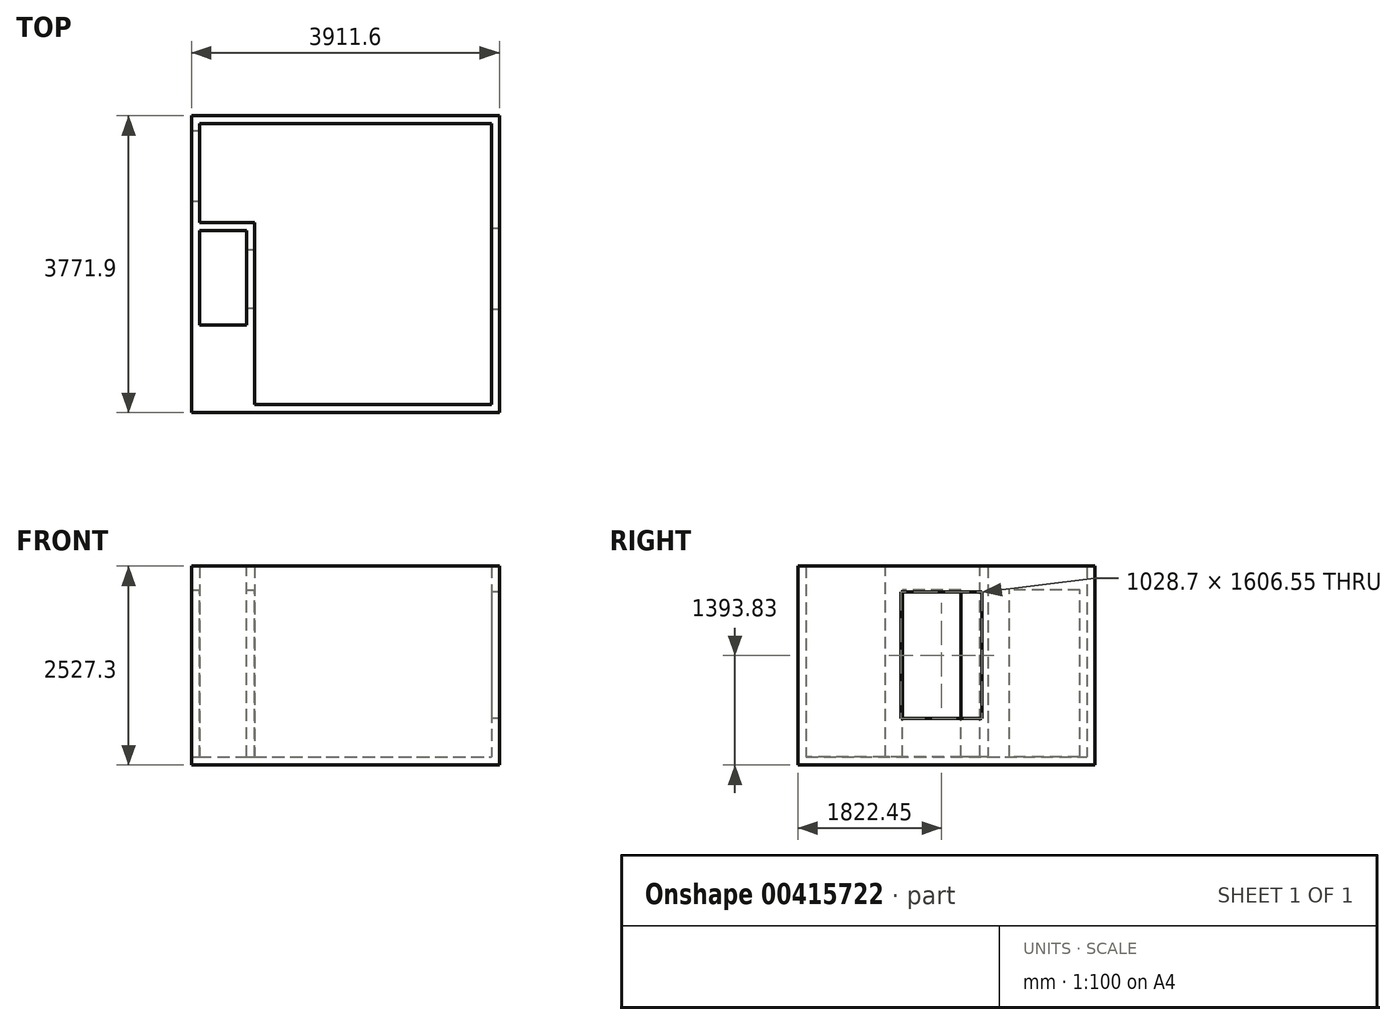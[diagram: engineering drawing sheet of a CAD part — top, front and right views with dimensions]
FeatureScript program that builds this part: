
annotation { "Feature Type Name" : "Feature", "Feature Type Description" : "" }
export const myFeature = defineFeature(function(context is Context, id is Id, definition is map)
    precondition{}
    {
        {
            var Q0;
            Q0=qCreatedBy(makeId("Top.planeOp"),FACE);
            var sketch = newSketch(context, id + "F0", { "sketchPlane" : qUnion([Q0])});
            skLineSegment(sketch, "E0.bottom", {"start": v(701.67, 0) * mm, "end": v(3708.4, 0) * mm});
            skLineSegment(sketch, "E0.top", {"start": v(0, 3568.7) * mm, "end": v(3708.4, 3568.7) * mm});
            skLineSegment(sketch, "E0.left", {"start": v(0, 2314.58) * mm, "end": v(0, 3568.7) * mm});
            skLineSegment(sketch, "E0.right", {"start": v(3708.4, 0) * mm, "end": v(3708.4, 3568.7) * mm});
            skLineSegment(sketch, "E1.0", {"start": v(-101.6, -101.6) * mm, "end": v(-101.6, 3670.3) * mm});
            skLineSegment(sketch, "E1.1", {"start": v(-101.6, -101.6) * mm, "end": v(3810, -101.6) * mm});
            skLineSegment(sketch, "E1.2", {"start": v(3810, -101.6) * mm, "end": v(3810, 3670.3) * mm});
            skLineSegment(sketch, "E1.3", {"start": v(-101.6, 3670.3) * mm, "end": v(3810, 3670.3) * mm});
            skLineSegment(sketch, "E2", {"start": v(0, 2314.58) * mm, "end": v(701.67, 2314.58) * mm});
            skLineSegment(sketch, "E3", {"start": v(701.67, 2314.58) * mm, "end": v(701.67, 0) * mm});
            skSolve(sketch);
        }
        {
            var Q0;
            Q0=qSketchRegion(id+"F0",true);
            extrude(context, id + "F1", {"entities" : qUnion([Q0]), "offsetDistance" : 25.4 * mm, "depth" : 2425.7 * mm});
        }
        {
            var Q0;
            Q0=makeQuery(id+"F1.opExtrude","CAP_FACE",FACE,{"disambiguationData":[OSD([sQuery(id+"F0.wireOp",EDGE,"E0.bottom"),sQuery(id+"F0.wireOp",EDGE,"E0.top"),sQuery(id+"F0.wireOp",EDGE,"E0.left"),sQuery(id+"F0.wireOp",EDGE,"E0.right"),sQuery(id+"F0.wireOp",EDGE,"E1.0"),sQuery(id+"F0.wireOp",EDGE,"E1.1"),sQuery(id+"F0.wireOp",EDGE,"E1.2"),sQuery(id+"F0.wireOp",EDGE,"E1.3")])],"isStart":true});
            var sketch = newSketch(context, id + "F2", { "sketchPlane" : qUnion([Q0])});
            skLineSegment(sketch, "E4.0", {"start": v(-101.6, 101.6) * mm, "end": v(3810, 101.6) * mm});
            skLineSegment(sketch, "E5.0", {"start": v(-101.6, 101.6) * mm, "end": v(-101.6, -3670.3) * mm});
            skLineSegment(sketch, "E6.0", {"start": v(-101.6, -3670.3) * mm, "end": v(3810, -3670.3) * mm});
            skLineSegment(sketch, "E7.0", {"start": v(3810, 101.6) * mm, "end": v(3810, -3670.3) * mm});
            skSolve(sketch);
        }
        {
            var Q0;
            Q0=qSketchRegion(id+"F2",true);
            extrude(context, id + "F3", {"entities" : qUnion([Q0]), "operationType" : NewBodyOperationType.ADD, "offsetDistance" : 25.4 * mm, "depth" : 101.6 * mm});
        }
        {
            var Q0;
            Q0=makeQuery(id+"F1.opExtrude","SWEPT_FACE",FACE,{"disambiguationData":[OSD([sQuery(id+"F0.wireOp",EDGE,"E0.left")])]});
            var sketch = newSketch(context, id + "F4", { "sketchPlane" : qUnion([Q0])});
            skLineSegment(sketch, "E8.bottom", {"start": v(3479.8, 0) * mm, "end": v(2584.45, 0) * mm});
            skLineSegment(sketch, "E8.top", {"start": v(3479.8, 2120.9) * mm, "end": v(2584.45, 2120.9) * mm});
            skLineSegment(sketch, "E8.left", {"start": v(3479.8, 0) * mm, "end": v(3479.8, 2120.9) * mm});
            skLineSegment(sketch, "E8.right", {"start": v(2584.45, 0) * mm, "end": v(2584.45, 2120.9) * mm});
            skSolve(sketch);
        }
        {
            var Q0;
            Q0=qSketchRegion(id+"F4",true);
            extrude(context, id + "F5", {"entities" : qUnion([Q0]), "operationType" : NewBodyOperationType.REMOVE, "endBound" : BoundingType.THROUGH_ALL, "oppositeDirection" : true, "offsetDistance" : 25.4 * mm, "depth" : 25.4 * mm});
        }
        {
            var Q0;
            Q0=makeQuery(id+"F1.opExtrude","SWEPT_FACE",FACE,{"disambiguationData":[OSD([sQuery(id+"F0.wireOp",EDGE,"E0.right")])]});
            var sketch = newSketch(context, id + "F6", { "sketchPlane" : qUnion([Q0])});
            skLineSegment(sketch, "E9.bottom", {"start": v(-2235.2, 2095.5) * mm, "end": v(-1206.5, 2095.5) * mm});
            skLineSegment(sketch, "E9.top", {"start": v(-2235.2, 488.95) * mm, "end": v(-1206.5, 488.95) * mm});
            skLineSegment(sketch, "E9.left", {"start": v(-2235.2, 2095.5) * mm, "end": v(-2235.2, 488.95) * mm});
            skLineSegment(sketch, "E9.right", {"start": v(-1206.5, 2095.5) * mm, "end": v(-1206.5, 488.95) * mm});
            skSolve(sketch);
        }
        {
            var Q0;
            Q0=qSketchRegion(id+"F6",true);
            extrude(context, id + "F7", {"entities" : qUnion([Q0]), "operationType" : NewBodyOperationType.REMOVE, "endBound" : BoundingType.THROUGH_ALL, "oppositeDirection" : true, "offsetDistance" : 25.4 * mm, "depth" : 25.4 * mm});
        }
        {
            var Q0;
            Q0=makeQuery(id+"F1.opExtrude","SWEPT_FACE",FACE,{"disambiguationData":[OSD([sQuery(id+"F0.wireOp",EDGE,"E3")])]});
            var sketch = newSketch(context, id + "F8", { "sketchPlane" : qUnion([Q0])});
            skLineSegment(sketch, "E10.bottom", {"start": v(1968.5, 0) * mm, "end": v(1228.73, 0) * mm});
            skLineSegment(sketch, "E10.top", {"start": v(1968.5, 2120.9) * mm, "end": v(1228.73, 2120.9) * mm});
            skLineSegment(sketch, "E10.left", {"start": v(1968.5, 0) * mm, "end": v(1968.5, 2120.9) * mm});
            skLineSegment(sketch, "E10.right", {"start": v(1228.73, 0) * mm, "end": v(1228.73, 2120.9) * mm});
            skSolve(sketch);
        }
        {
            var Q0;
            Q0 = qSketchRegion(id + "F8", true);
            extrude(context, id + "F9", {"entities" : qUnion([Q0]), "operationType" : NewBodyOperationType.REMOVE, "oppositeDirection" : true, "offsetDistance" : 25.4 * mm, "depth" : 101.6 * mm});
        }
        {
            var Q0;
            Q0=makeQuery(id+"F1.opExtrude","CAP_FACE",FACE,{"disambiguationData":[OSD([sQuery(id+"F0.wireOp",EDGE,"E0.bottom"),sQuery(id+"F0.wireOp",EDGE,"E0.top"),sQuery(id+"F0.wireOp",EDGE,"E0.left"),sQuery(id+"F0.wireOp",EDGE,"E0.right"),sQuery(id+"F0.wireOp",EDGE,"E1.0"),sQuery(id+"F0.wireOp",EDGE,"E1.1"),sQuery(id+"F0.wireOp",EDGE,"E1.2"),sQuery(id+"F0.wireOp",EDGE,"E1.3"),sQuery(id+"F0.wireOp",EDGE,"E2"),sQuery(id+"F0.wireOp",EDGE,"E3")])],"isStart":false});
            var sketch = newSketch(context, id + "F10", { "sketchPlane" : qUnion([Q0])});
            skLineSegment(sketch, "E11.bottom", {"start": v(0, 2212.98) * mm, "end": v(600.07, 2212.98) * mm});
            skLineSegment(sketch, "E11.top", {"start": v(0, 1012.83) * mm, "end": v(600.07, 1012.83) * mm});
            skLineSegment(sketch, "E11.left", {"start": v(0, 2212.98) * mm, "end": v(0, 1012.83) * mm});
            skLineSegment(sketch, "E11.right", {"start": v(600.07, 2212.98) * mm, "end": v(600.07, 1012.83) * mm});
            skSolve(sketch);
        }
        {
            var Q0;
            Q0 = qSketchRegion(id + "F10", true);
            var Q1;
            Q1=makeQuery(id+"F9.boolean.opBoolean","MERGE",FACE,{"derivedFrom":[makeQuery(id+"F5.boolean.opBoolean","MERGE",FACE,{"derivedFrom":[makeQuery(id+"F3.opExtrude","CAP_FACE",FACE,{"disambiguationData":[OSD([sQuery(id+"F2.wireOp",EDGE,"E4.0"),sQuery(id+"F2.wireOp",EDGE,"E5.0"),sQuery(id+"F2.wireOp",EDGE,"E6.0"),sQuery(id+"F2.wireOp",EDGE,"E7.0")])],"isStart":true}),makeQuery(id+"F5.opExtrude","SWEPT_FACE",FACE,{"disambiguationData":[OSD([sQuery(id+"F4.wireOp",EDGE,"E8.bottom")])]})]}),makeQuery(id+"F9.opExtrude","SWEPT_FACE",FACE,{"disambiguationData":[OSD([sQuery(id+"F8.wireOp",EDGE,"E10.bottom")])]})]});
            extrude(context, id + "F11", {"entities" : qUnion([Q0]), "operationType" : NewBodyOperationType.REMOVE, "endBound" : BoundingType.UP_TO_SURFACE, "oppositeDirection" : true, "endBoundEntityFace" : qUnion([Q1]), "offsetDistance" : 25.4 * mm, "depth" : 25.4 * mm});
        }
    });
